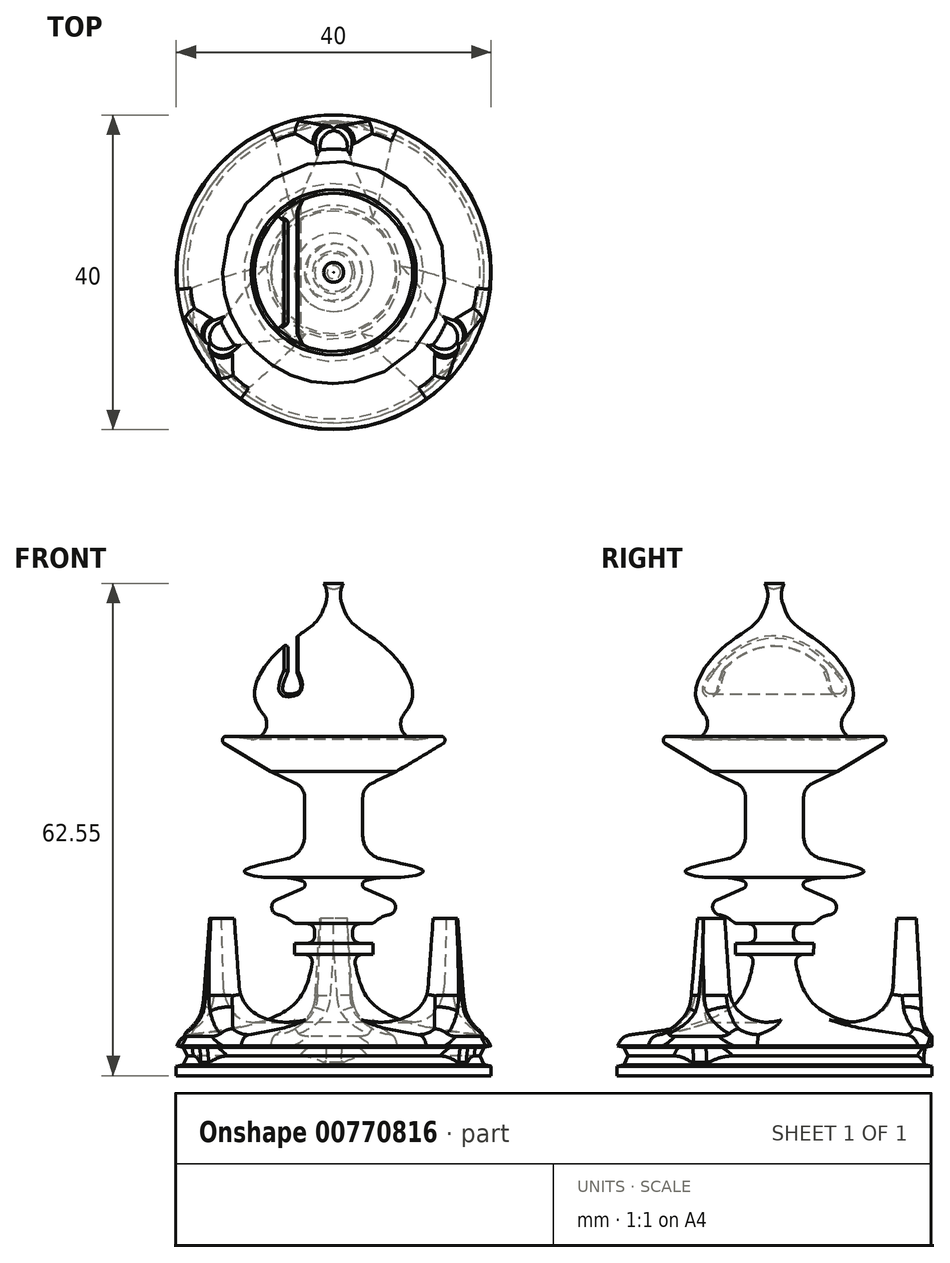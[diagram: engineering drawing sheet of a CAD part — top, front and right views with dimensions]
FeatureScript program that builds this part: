
annotation { "Feature Type Name" : "Feature", "Feature Type Description" : "" }
export const myFeature = defineFeature(function(context is Context, id is Id, definition is map)
    precondition{}
    {
        {
            var Q0;
            Q0=qCreatedBy(makeId("Front.planeOp"),FACE);
            var sketch = newSketch(context, id + "F0", { "sketchPlane" : qUnion([Q0])});
            skLineSegment(sketch, "E0.bottom", {"start": v(0, 0) * mm, "end": v(20, 0) * mm});
            skLineSegment(sketch, "E0.right", {"start": v(20, 0) * mm, "end": v(20, 1.23) * mm});
            skFitSpline(sketch, "E1", {"points": [v(20, 5) * mm, v(5.27, 8.84) * mm, v(2.52, 15.41) * mm], "startDerivative": vector(-30.16, 3.58) * mm, "endDerivative": vector(-3.11, 18.15) * mm});
            skLineSegment(sketch, "E2.bottom", {"start": v(2.52, 15.41) * mm, "end": v(4.97, 15.41) * mm});
            skLineSegment(sketch, "E2.right", {"start": v(4.97, 15.41) * mm, "end": v(4.97, 16.8) * mm});
            skLineSegment(sketch, "E3", {"start": v(6.26, 20.35) * mm, "end": v(10.63, 20.86) * mm});
            skLineSegment(sketch, "E4", {"start": v(10.63, 20.86) * mm, "end": v(2.82, 24.3) * mm});
            skFitSpline(sketch, "E5", {"points": [v(2.82, 24.3) * mm, v(8.68, 25.2) * mm, v(11.36, 26) * mm, v(5.8, 27.58) * mm, v(3.7, 28.85) * mm, v(2.82, 33.13) * mm, v(-32.06, 38.18) * mm], "startDerivative": vector(58.6, 24.99) * mm, "endDerivative": vector(-147.9, 1.56) * mm});
            skLineSegment(sketch, "E6", {"start": v(3.7, 28.85) * mm, "end": v(3.7, 36.6) * mm});
            skLineSegment(sketch, "E7", {"start": v(0, 50.21) * mm, "end": v(0, 0) * mm});
            skLineSegment(sketch, "E8", {"start": v(4.97, 16.8) * mm, "end": v(2.4, 16.82) * mm});
            skLineSegment(sketch, "E9", {"start": v(2.4, 16.82) * mm, "end": v(2.4, 19.32) * mm});
            skLineSegment(sketch, "E10", {"start": v(2.4, 19.32) * mm, "end": v(4.97, 19.32) * mm});
            skLineSegment(sketch, "E11", {"start": v(4.97, 19.32) * mm, "end": v(6.26, 20.35) * mm});
            skLineSegment(sketch, "E12", {"start": v(3.7, 36.6) * mm, "end": v(8, 38.66) * mm});
            skLineSegment(sketch, "E13", {"start": v(8, 38.66) * mm, "end": v(15.99, 43.44) * mm});
            skLineSegment(sketch, "E14", {"start": v(15.99, 43.44) * mm, "end": v(10.49, 42.7) * mm});
            skLineSegment(sketch, "E15", {"start": v(10.49, 42.7) * mm, "end": v(5.23, 42.69) * mm});
            skFitSpline(sketch, "E16", {"points": [v(5.23, 42.69) * mm, v(10.04, 48.36) * mm, v(6.28, 54.6) * mm, v(2.2, 57.7) * mm, v(0.83, 60.64) * mm, v(0, 64.74) * mm], "startDerivative": vector(29.47, 22.4) * mm, "endDerivative": vector(-0.1, 24.57) * mm});
            skLineSegment(sketch, "E17", {"start": v(0, 64.74) * mm, "end": v(0, 0) * mm});
            skArc(sketch, "E18.cCircle", {"start": v(20, 3.77) * mm, "mid": v(18.73, 2.5) * mm, "end": v(20, 1.23) * mm, "construction": true});
            skLineSegment(sketch, "E18.2", {"start": v(20, 1.2) * mm, "end": v(19.12, 1.4) * mm});
            skLineSegment(sketch, "E18.3", {"start": v(19.12, 1.4) * mm, "end": v(18.6, 2.5) * mm});
            skLineSegment(sketch, "E18.4", {"start": v(18.6, 2.5) * mm, "end": v(19.12, 3.6) * mm});
            skLineSegment(sketch, "E18.5", {"start": v(19.12, 3.6) * mm, "end": v(20, 3.8) * mm});
            skPoint(sketch, "E18.0.midPoint", {"position": v(21.27, 2.5) * mm});
            skPoint(sketch, "E19.orphan", {"position": v(21.27, 3.11) * mm});
            skPoint(sketch, "E18.0.end.orphan", {"position": v(21.27, 1.89) * mm});
            skPoint(sketch, "E20.orphan", {"position": v(20.31, 1.13) * mm});
            skLineSegment(sketch, "E21.trimOffspring", {"start": v(20, 3.77) * mm, "end": v(20, 5) * mm});
            skArc(sketch, "E22", {"start": v(0.45, 61.9) * mm, "mid": v(1.44, 63.51) * mm, "end": v(0, 64.74) * mm});
            skSolve(sketch);
        }
        {
            var Q0;
            Q0 = qSketchRegion(id + "F0", true);
            var Q1;
            Q1=sQuery(id+"F0.wireOp",EDGE,"E7");
            revolve(context, id + "F1", {"surfaceOperationType" : NewSurfaceOperationType.NEW, "entities" : qUnion([Q0]), "axis" : qUnion([Q1]), "revolveType" : RevolveType.FULL});
        }
        {
            var Q0;
            Q0=makeQuery(id+"F1.opRevolve","SWEPT_EDGE",EDGE,{"disambiguationData":[OSD([sQuery(id+"F0.wireOp",EDGE,"E1"),sQuery(id+"F0.wireOp",EDGE,"E2.bottom")])]});
            fillet(context, id + "F2", {"entities" : qUnion([Q0]), "radius" : 1 * mm, "tangentPropagation" : true, "allowEdgeOverflow" : false});
        }
        {
            var Q0;
            Q0=makeQuery(id+"F1.opRevolve","SWEPT_EDGE",EDGE,{"disambiguationData":[OSD([sQuery(id+"F0.wireOp",EDGE,"E8"),sQuery(id+"F0.wireOp",EDGE,"E9")])]});
            fillet(context, id + "F3", {"entities" : qUnion([Q0]), "radius" : 1 * mm, "tangentPropagation" : true, "allowEdgeOverflow" : false});
        }
        {
            var Q0;
            Q0=makeQuery(id+"F1.opRevolve","SWEPT_EDGE",EDGE,{"disambiguationData":[OSD([sQuery(id+"F0.wireOp",EDGE,"E9"),sQuery(id+"F0.wireOp",EDGE,"E10")])]});
            fillet(context, id + "F4", {"entities" : qUnion([Q0]), "radius" : 1 * mm, "tangentPropagation" : true, "allowEdgeOverflow" : false});
        }
        {
            var Q0;
            Q0=makeQuery(id+"F1.opRevolve","SWEPT_EDGE",EDGE,{"disambiguationData":[OSD([sQuery(id+"F0.wireOp",EDGE,"E10"),sQuery(id+"F0.wireOp",EDGE,"E11")])]});
            fillet(context, id + "F5", {"entities" : qUnion([Q0]), "radius" : 1 * mm, "tangentPropagation" : true, "allowEdgeOverflow" : false});
        }
        {
            var Q0;
            Q0=makeQuery(id+"F1.opRevolve","SWEPT_EDGE",EDGE,{"disambiguationData":[OSD([sQuery(id+"F0.wireOp",EDGE,"E3"),sQuery(id+"F0.wireOp",EDGE,"E11")])]});
            fillet(context, id + "F6", {"entities" : qUnion([Q0]), "radius" : 3 * mm, "tangentPropagation" : true, "allowEdgeOverflow" : false});
        }
        {
            var Q0;
            Q0=makeQuery(id+"F1.opRevolve","SWEPT_EDGE",EDGE,{"disambiguationData":[OSD([sQuery(id+"F0.wireOp",EDGE,"E3"),sQuery(id+"F0.wireOp",EDGE,"E4")])]});
            fillet(context, id + "F7", {"entities" : qUnion([Q0]), "radius" : 1 * mm, "tangentPropagation" : true, "allowEdgeOverflow" : false});
        }
        {
            var Q0;
            Q0=makeQuery(id+"F1.opRevolve","SWEPT_EDGE",EDGE,{"disambiguationData":[OSD([sQuery(id+"F0.wireOp",EDGE,"E4"),sQuery(id+"F0.wireOp",EDGE,"E5")])]});
            fillet(context, id + "F8", {"entities" : qUnion([Q0]), "radius" : .5 * mm, "tangentPropagation" : true, "allowEdgeOverflow" : false});
        }
        {
            var Q0;
            Q0=makeQuery(id+"F1.opRevolve","SWEPT_EDGE",EDGE,{"disambiguationData":[OSD([sQuery(id+"F0.wireOp",EDGE,"E6"),sQuery(id+"F0.wireOp",EDGE,"E12")])]});
            fillet(context, id + "F9", {"entities" : qUnion([Q0]), "radius" : 2 * mm, "tangentPropagation" : true, "allowEdgeOverflow" : false});
        }
        {
            var Q0;
            Q0=makeQuery(id+"F1.opRevolve","SWEPT_EDGE",EDGE,{"disambiguationData":[OSD([sQuery(id+"F0.wireOp",EDGE,"E5"),sQuery(id+"F0.wireOp",EDGE,"E6")])]});
            fillet(context, id + "F10", {"entities" : qUnion([Q0]), "radius" : 3 * mm, "tangentPropagation" : true, "allowEdgeOverflow" : false});
        }
        {
            var Q0;
            Q0=makeQuery(id+"F1.opRevolve","SWEPT_EDGE",EDGE,{"disambiguationData":[OSD([sQuery(id+"F0.wireOp",EDGE,"E15"),sQuery(id+"F0.wireOp",EDGE,"E16")])]});
            fillet(context, id + "F11", {"entities" : qUnion([Q0]), "radius" : 2 * mm, "tangentPropagation" : true, "allowEdgeOverflow" : false});
        }
        {
            var Q0;
            Q0=qCreatedBy(makeId("Top.planeOp"),FACE);
            var sketch = newSketch(context, id + "F12", { "sketchPlane" : qUnion([Q0])});
            skLineSegment(sketch, "E23", {"start": v(2.53, 14.37) * mm, "end": v(3.31, 18.78) * mm});
            skLineSegment(sketch, "E24", {"start": v(-2.53, 14.37) * mm, "end": v(-3.31, 18.78) * mm});
            skArc(sketch, "E25", {"start": v(2.53, 14.37) * mm, "mid": v(0, 14.6) * mm, "end": v(-2.53, 14.37) * mm});
            skArc(sketch, "E26", {"start": v(3.31, 18.78) * mm, "mid": v(0, 19.07) * mm, "end": v(-3.31, 18.78) * mm});
            skLineSegment(sketch, "E27.1.0", {"start": v(-11.18, -9.38) * mm, "end": v(-14.6, -12.26) * mm});
            skArc(sketch, "E27.1.1", {"start": v(-17.92, -6.52) * mm, "mid": v(-16.52, -9.54) * mm, "end": v(-14.6, -12.26) * mm});
            skArc(sketch, "E27.1.2", {"start": v(-13.72, -5) * mm, "mid": v(-12.64, -7.3) * mm, "end": v(-11.18, -9.38) * mm});
            skLineSegment(sketch, "E27.1.3", {"start": v(-13.72, -5) * mm, "end": v(-17.92, -6.52) * mm});
            skLineSegment(sketch, "E27.2.0", {"start": v(13.72, -5) * mm, "end": v(17.92, -6.52) * mm});
            skArc(sketch, "E27.2.1", {"start": v(14.6, -12.26) * mm, "mid": v(16.52, -9.54) * mm, "end": v(17.92, -6.52) * mm});
            skArc(sketch, "E27.2.2", {"start": v(11.18, -9.38) * mm, "mid": v(12.64, -7.3) * mm, "end": v(13.72, -5) * mm});
            skLineSegment(sketch, "E27.2.3", {"start": v(11.18, -9.38) * mm, "end": v(14.6, -12.26) * mm});
            skSolve(sketch);
        }
        {
            var Q0;
            Q0 = qSketchRegion(id + "F12", true);
            extrude(context, id + "F13", {"entities" : qUnion([Q0]), "operationType" : NewBodyOperationType.ADD, "depth" : 20 * mm, "offsetDistance" : 25 * mm, "hasDraft" : true, "draftAngle" : 3 * degree, "draftPullDirection" : true});
        }
        {
            var Q0;
            Q0=makeQuery(id+"F1.opRevolve","SWEPT_EDGE",EDGE,{"disambiguationData":[OSD([sQuery(id+"F0.wireOp",EDGE,"E13"),sQuery(id+"F0.wireOp",EDGE,"E14")])]});
            fillet(context, id + "F14", {"entities" : qUnion([Q0]), "radius" : .5 * mm, "tangentPropagation" : true, "allowEdgeOverflow" : false});
        }
        {
            var Q0;
            Q0=makeQuery(id+"F13.boolean.opBoolean","INTERSECT",EDGE,{"derivedFrom":[makeQuery(id+"F1.opRevolve","SWEPT_FACE",FACE,{"disambiguationData":[OSD([sQuery(id+"F0.wireOp",EDGE,"E1")])]}),makeQuery(id+"F13.opExtrude","SWEPT_FACE",FACE,{"disambiguationData":[OSD([sQuery(id+"F12.wireOp",EDGE,"E27.1.3")])]})]});
            var Q1;
            Q1=makeQuery(id+"F13.boolean.opBoolean","INTERSECT",EDGE,{"derivedFrom":[makeQuery(id+"F1.opRevolve","SWEPT_FACE",FACE,{"disambiguationData":[OSD([sQuery(id+"F0.wireOp",EDGE,"E1")])]}),makeQuery(id+"F13.opExtrude","SWEPT_FACE",FACE,{"disambiguationData":[OSD([sQuery(id+"F12.wireOp",EDGE,"E27.1.1")])]})]});
            var Q2;
            Q2=makeQuery(id+"F13.boolean.opBoolean","INTERSECT",EDGE,{"derivedFrom":[makeQuery(id+"F1.opRevolve","SWEPT_FACE",FACE,{"disambiguationData":[OSD([sQuery(id+"F0.wireOp",EDGE,"E1")])]}),makeQuery(id+"F13.opExtrude","SWEPT_FACE",FACE,{"disambiguationData":[OSD([sQuery(id+"F12.wireOp",EDGE,"E27.1.0")])]})]});
            var Q3;
            Q3=makeQuery(id+"F13.boolean.opBoolean","INTERSECT",EDGE,{"derivedFrom":[makeQuery(id+"F1.opRevolve","SWEPT_FACE",FACE,{"disambiguationData":[OSD([sQuery(id+"F0.wireOp",EDGE,"E1")])]}),makeQuery(id+"F13.opExtrude","SWEPT_FACE",FACE,{"disambiguationData":[OSD([sQuery(id+"F12.wireOp",EDGE,"E27.1.2")])]})]});
            var Q4;
            Q4=makeQuery(id+"F13.boolean.opBoolean","INTERSECT",EDGE,{"derivedFrom":[makeQuery(id+"F1.opRevolve","SWEPT_FACE",FACE,{"disambiguationData":[OSD([sQuery(id+"F0.wireOp",EDGE,"E1")])]}),makeQuery(id+"F13.opExtrude","SWEPT_FACE",FACE,{"disambiguationData":[OSD([sQuery(id+"F12.wireOp",EDGE,"E27.2.1")])]})]});
            var Q5;
            Q5=makeQuery(id+"F13.boolean.opBoolean","INTERSECT",EDGE,{"derivedFrom":[makeQuery(id+"F1.opRevolve","SWEPT_FACE",FACE,{"disambiguationData":[OSD([sQuery(id+"F0.wireOp",EDGE,"E1")])]}),makeQuery(id+"F13.opExtrude","SWEPT_FACE",FACE,{"disambiguationData":[OSD([sQuery(id+"F12.wireOp",EDGE,"E27.2.0")])]})]});
            var Q6;
            Q6=makeQuery(id+"F13.boolean.opBoolean","INTERSECT",EDGE,{"derivedFrom":[makeQuery(id+"F1.opRevolve","SWEPT_FACE",FACE,{"disambiguationData":[OSD([sQuery(id+"F0.wireOp",EDGE,"E1")])]}),makeQuery(id+"F13.opExtrude","SWEPT_FACE",FACE,{"disambiguationData":[OSD([sQuery(id+"F12.wireOp",EDGE,"E27.2.3")])]})]});
            var Q7;
            Q7=makeQuery(id+"F13.boolean.opBoolean","INTERSECT",EDGE,{"derivedFrom":[makeQuery(id+"F1.opRevolve","SWEPT_FACE",FACE,{"disambiguationData":[OSD([sQuery(id+"F0.wireOp",EDGE,"E1")])]}),makeQuery(id+"F13.opExtrude","SWEPT_FACE",FACE,{"disambiguationData":[OSD([sQuery(id+"F12.wireOp",EDGE,"E27.2.2")])]})]});
            var Q8;
            Q8=makeQuery(id+"F13.boolean.opBoolean","INTERSECT",EDGE,{"derivedFrom":[makeQuery(id+"F1.opRevolve","SWEPT_FACE",FACE,{"disambiguationData":[OSD([sQuery(id+"F0.wireOp",EDGE,"E1")])]}),makeQuery(id+"F13.opExtrude","SWEPT_FACE",FACE,{"disambiguationData":[OSD([sQuery(id+"F12.wireOp",EDGE,"E24")])]})]});
            var Q9;
            Q9=makeQuery(id+"F13.boolean.opBoolean","INTERSECT",EDGE,{"derivedFrom":[makeQuery(id+"F1.opRevolve","SWEPT_FACE",FACE,{"disambiguationData":[OSD([sQuery(id+"F0.wireOp",EDGE,"E1")])]}),makeQuery(id+"F13.opExtrude","SWEPT_FACE",FACE,{"disambiguationData":[OSD([sQuery(id+"F12.wireOp",EDGE,"E26")])]})]});
            var Q10;
            Q10=makeQuery(id+"F13.boolean.opBoolean","INTERSECT",EDGE,{"derivedFrom":[makeQuery(id+"F1.opRevolve","SWEPT_FACE",FACE,{"disambiguationData":[OSD([sQuery(id+"F0.wireOp",EDGE,"E1")])]}),makeQuery(id+"F13.opExtrude","SWEPT_FACE",FACE,{"disambiguationData":[OSD([sQuery(id+"F12.wireOp",EDGE,"E25")])]})]});
            var Q11;
            Q11=makeQuery(id+"F13.boolean.opBoolean","INTERSECT",EDGE,{"derivedFrom":[makeQuery(id+"F1.opRevolve","SWEPT_FACE",FACE,{"disambiguationData":[OSD([sQuery(id+"F0.wireOp",EDGE,"E1")])]}),makeQuery(id+"F13.opExtrude","SWEPT_FACE",FACE,{"disambiguationData":[OSD([sQuery(id+"F12.wireOp",EDGE,"E23")])]})]});
            fillet(context, id + "F15", {"entities" : qUnion([Q0, Q1, Q2, Q3, Q4, Q5, Q6, Q7, Q8, Q9, Q10, Q11]), "radius" : 5 * mm, "tangentPropagation" : true, "allowEdgeOverflow" : false});
        }
        {
            var Q0;
            Q0=makeQuery(id+"F13.opExtrude","SWEPT_EDGE",EDGE,{"disambiguationData":[OSD([sQuery(id+"F12.wireOp",EDGE,"E23"),sQuery(id+"F12.wireOp",EDGE,"E26")])]});
            var Q1;
            Q1=makeQuery(id+"F13.opExtrude","SWEPT_EDGE",EDGE,{"disambiguationData":[OSD([sQuery(id+"F12.wireOp",EDGE,"E24"),sQuery(id+"F12.wireOp",EDGE,"E26")])]});
            var Q2;
            Q2=makeQuery(id+"F13.opExtrude","SWEPT_EDGE",EDGE,{"disambiguationData":[OSD([sQuery(id+"F12.wireOp",EDGE,"E27.1.0"),sQuery(id+"F12.wireOp",EDGE,"E27.1.1")])]});
            var Q3;
            Q3=makeQuery(id+"F13.opExtrude","SWEPT_EDGE",EDGE,{"disambiguationData":[OSD([sQuery(id+"F12.wireOp",EDGE,"E27.2.1"),sQuery(id+"F12.wireOp",EDGE,"E27.2.3")])]});
            var Q4;
            Q4=makeQuery(id+"F13.opExtrude","SWEPT_EDGE",EDGE,{"disambiguationData":[OSD([sQuery(id+"F12.wireOp",EDGE,"E27.2.0"),sQuery(id+"F12.wireOp",EDGE,"E27.2.1")])]});
            var Q5;
            Q5=makeQuery(id+"F13.opExtrude","SWEPT_EDGE",EDGE,{"disambiguationData":[OSD([sQuery(id+"F12.wireOp",EDGE,"E27.1.1"),sQuery(id+"F12.wireOp",EDGE,"E27.1.3")])]});
            fillet(context, id + "F16", {"entities" : qUnion([Q0, Q1, Q2, Q3, Q4, Q5]), "radius" : 2 * mm, "tangentPropagation" : true, "allowEdgeOverflow" : false});
        }
        {
            var Q0;
            Q0=qCreatedBy(makeId("Front.planeOp"),FACE);
            var sketch = newSketch(context, id + "F17", { "sketchPlane" : qUnion([Q0])});
            skLineSegment(sketch, "E28.bottom", {"start": v(-4.67, 55.86) * mm, "end": v(-5.81, 55.86) * mm});
            skLineSegment(sketch, "E28.left", {"start": v(-4.67, 55.86) * mm, "end": v(-4.67, 51.2) * mm});
            skLineSegment(sketch, "E28.right", {"start": v(-5.81, 55.86) * mm, "end": v(-5.81, 51.3) * mm});
            skFitSpline(sketch, "E29", {"points": [v(-4.67, 51.2) * mm, v(-4.15, 49.44) * mm, v(-4.67, 48.66) * mm, v(-6.33, 48.71) * mm, v(-5.81, 51.3) * mm], "startDerivative": vector(3.07, -7.4) * mm, "endDerivative": vector(4.44, 10.42) * mm});
            skPoint(sketch, "E28.top.start.orphan", {"position": v(-4.67, 49.44) * mm});
            skSolve(sketch);
        }
        {
            var Q0;
            Q0 = qSketchRegion(id + "F17", true);
            extrude(context, id + "F18", {"entities" : qUnion([Q0]), "operationType" : NewBodyOperationType.REMOVE, "endBound" : BoundingType.SYMMETRIC, "oppositeDirection" : true, "depth" : 25 * mm, "offsetDistance" : 25 * mm});
        }
        {
            var Q0;
            Q0=makeQuery(id+"F18.boolean.opBoolean","INTERSECT",EDGE,{"disambiguationData":[OD(0.0)],"derivedFrom":[makeQuery(id+"F1.opRevolve","SWEPT_FACE",FACE,{"disambiguationData":[OSD([sQuery(id+"F0.wireOp",EDGE,"E16")])]}),makeQuery(id+"F18.opExtrude","SWEPT_FACE",FACE,{"disambiguationData":[OSD([sQuery(id+"F17.wireOp",EDGE,"E29")])]})]});
            fillet(context, id + "F19", {"entities" : qUnion([Q0]), "radius" : .3 * mm, "tangentPropagation" : true, "allowEdgeOverflow" : false});
        }
        {
            var Q0;
            Q0=makeQuery(id+"F18.boolean.opBoolean","INTERSECT",EDGE,{"disambiguationData":[OD(1.0)],"derivedFrom":[makeQuery(id+"F1.opRevolve","SWEPT_FACE",FACE,{"disambiguationData":[OSD([sQuery(id+"F0.wireOp",EDGE,"E16")])]}),makeQuery(id+"F18.opExtrude","SWEPT_FACE",FACE,{"disambiguationData":[OSD([sQuery(id+"F17.wireOp",EDGE,"E29")])]})]});
            fillet(context, id + "F20", {"entities" : qUnion([Q0]), "radius" : .3 * mm, "tangentPropagation" : true, "allowEdgeOverflow" : false});
        }
        {
            var Q0;
            Q0=makeQuery(id+"F18.boolean.opBoolean","COPY",EDGE,{"derivedFrom":makeQuery(id+"F18.opExtrude","SWEPT_EDGE",EDGE,{"disambiguationData":[OSD([sQuery(id+"F17.wireOp",EDGE,"E28.right"),sQuery(id+"F17.wireOp",EDGE,"E29")])]})});
            var Q1;
            Q1=makeQuery(id+"F18.boolean.opBoolean","INTERSECT",EDGE,{"derivedFrom":[makeQuery(id+"F1.opRevolve","SWEPT_FACE",FACE,{"disambiguationData":[OSD([sQuery(id+"F0.wireOp",EDGE,"E16")])]}),makeQuery(id+"F18.opExtrude","SWEPT_FACE",FACE,{"disambiguationData":[OSD([sQuery(id+"F17.wireOp",EDGE,"E28.left")])]})]});
            var Q2;
            Q2=makeQuery(id+"F18.boolean.opBoolean","COPY",EDGE,{"derivedFrom":makeQuery(id+"F18.opExtrude","SWEPT_EDGE",EDGE,{"disambiguationData":[OSD([sQuery(id+"F17.wireOp",EDGE,"E28.left"),sQuery(id+"F17.wireOp",EDGE,"E29")])]})});
            var Q3;
            Q3=makeQuery(id+"F18.boolean.opBoolean","INTERSECT",EDGE,{"derivedFrom":[makeQuery(id+"F1.opRevolve","SWEPT_FACE",FACE,{"disambiguationData":[OSD([sQuery(id+"F0.wireOp",EDGE,"E16")])]}),makeQuery(id+"F18.opExtrude","SWEPT_FACE",FACE,{"disambiguationData":[OSD([sQuery(id+"F17.wireOp",EDGE,"E28.right")])]})]});
            fillet(context, id + "F21", {"entities" : qUnion([Q0, Q1, Q2, Q3]), "radius" : .3 * mm, "tangentPropagation" : true, "allowEdgeOverflow" : false});
        }
        {
            var Q0;
            Q0=makeQuery(id+"F13.boolean.opBoolean","INTERSECT",EDGE,{"derivedFrom":[makeQuery(id+"F1.opRevolve","SWEPT_FACE",FACE,{"disambiguationData":[OSD([sQuery(id+"F0.wireOp",EDGE,"E18.4")])]}),makeQuery(id+"F13.opExtrude","SWEPT_FACE",FACE,{"disambiguationData":[OSD([sQuery(id+"F12.wireOp",EDGE,"E27.2.1")])]})]});
            var Q1;
            Q1=makeQuery(id+"F13.boolean.opBoolean","INTERSECT",EDGE,{"derivedFrom":[makeQuery(id+"F1.opRevolve","SWEPT_FACE",FACE,{"disambiguationData":[OSD([sQuery(id+"F0.wireOp",EDGE,"E18.4")])]}),makeQuery(id+"F13.opExtrude","SWEPT_FACE",FACE,{"disambiguationData":[OSD([sQuery(id+"F12.wireOp",EDGE,"E27.1.1")])]})]});
            var Q2;
            Q2=makeQuery(id+"F13.boolean.opBoolean","INTERSECT",EDGE,{"derivedFrom":[makeQuery(id+"F1.opRevolve","SWEPT_FACE",FACE,{"disambiguationData":[OSD([sQuery(id+"F0.wireOp",EDGE,"E18.4")])]}),makeQuery(id+"F13.opExtrude","SWEPT_FACE",FACE,{"disambiguationData":[OSD([sQuery(id+"F12.wireOp",EDGE,"E26")])]})]});
            fillet(context, id + "F22", {"entities" : qUnion([Q0, Q1, Q2]), "radius" : 5 * mm, "tangentPropagation" : true, "allowEdgeOverflow" : false});
        }
        {
            var Q0;
            Q0=makeQuery(id+"F1.opRevolve","SWEPT_EDGE",EDGE,{"disambiguationData":[OSD([sQuery(id+"F0.wireOp",EDGE,"E16"),sQuery(id+"F0.wireOp",EDGE,"E22")])]});
            fillet(context, id + "F23", {"entities" : qUnion([Q0]), "radius" : 3 * mm, "tangentPropagation" : true, "allowEdgeOverflow" : false});
        }
    });
